# Revit family: Drain_Floor_12-Inch-Round_Zurn-Z1736_Extra-Heavy-Duty
name_source: partatom
category: Plumbing Fixtures
units: mm (PartAtom-declared; Revit-internal decimal feet)

## family parameters
Always vertical = Yes
Cut with Voids When Loaded = No
Maintain Annotation Orientation = No
OmniClass Number = 23.45.55.21
OmniClass Title = Drains (Wastes)
Part Type = Normal
Room Calculation Point = No
Round Connector Dimension = Use Radius
Shared = No
Work Plane-Based = No

## types (12) — shared parameters
Approx. Weight (Lbs) = 61 "
Assembly Code = D2030300
CW Connection = No
Default Elevation = 20 "
Description = 12 INCH DIAMETER EXTRA HEAVY-DUTY FLOOR DRAIN
Grate Open Area (Sq. In.) = 34 "
HW Connection = No
Manufacturer = Zurn Water, LLC
Manufacurer Brand = Zurn
Modified Date = 11/14/25
Product Documentation Link = https://files.zurn.com
Product Page URL = https://www.zurn.com
Product data url = https://www.bimobject.com
URL = www.zurn.com
Vent Connection = No
Waste Connection = Yes
zero-valued in all types: CWFU, HWFU, WFU

## per-type parameters (varying)
| type | Body HT Dim 'E' | Main Material | Model | Pipe Size 'A' (Inner Diameter) | Pipe Size 'A' (Inner Radius) | Pipe Size 'A' (Nominal Diameter) | Pipe Size 'A' (Nominal Radius) | Pipe Size 'A' (Outer Diameter) | Pipe Size 'A' (Outer Radius) | Type Comments |
| Z1736-3BW | 6 " | Steel - Zurn - Stainless - Type - 304 | Z1736 | 3.069 " | 1.535 " | 3 " | 1.5 " | 3.5 " | 1.75 " | Z1736 - 3 Inch Butt-Weld Outlet |
| Z1736-3IP | 6.082 " | Steel - Zurn - Stainless - Type - 304 | Z1736 | 3.069 " | 1.535 " | 3 " | 1.5 " | 3.5 " | 1.75 " | Z1736 - 3 Inch IP Threaded Outlet |
| Z1736-4BW | 6 " | Steel - Zurn - Stainless - Type - 304 | Z1736 | 4.026 " | 2.013 " | 4 " | 2 " | 4.5 " | 2.25 " | Z1736 - 4 Inch Butt-Weld Outlet |
| Z1736-4IP | 6.082 " | Steel - Zurn - Stainless - Type - 304 | Z1736 | 4.026 " | 2.013 " | 4 " | 2 " | 4.5 " | 2.25 " | Z1736 - 4 Inch IP Threaded Outlet |
| Z1736-6BW | 6 " | Steel - Zurn - Stainless - Type - 304 | Z1736 | 6.065 " | 3.033 " | 6 " | 3 " | 6.625 " | 3.313 " | Z1736 - 6 Inch Butt-Weld Outlet |
| Z1736-6IP | 6.082 " | Steel - Zurn - Stainless - Type - 304 | Z1736 | 6.065 " | 3.033 " | 6 " | 3 " | 6.625 " | 3.313 " | Z1736 - 6 Inch IP Threaded Outlet |
| ZM1736-3BW | 6 " | Steel - Zurn- Stainless - Type - 316 | ZM1736 | 3.069 " | 1.535 " | 3 " | 1.5 " | 3.5 " | 1.75 " | ZM1736 - 3 Inch Butt-Weld Outlet |
| ZM1736-3IP | 6.082 " | Steel - Zurn- Stainless - Type - 316 | ZM1736 | 3.069 " | 1.535 " | 3 " | 1.5 " | 3.5 " | 1.75 " | ZM1736 - 3 Inch IP Threaded Outlet |
| ZM1736-4BW | 6 " | Steel - Zurn- Stainless - Type - 316 | ZM1736 | 4.026 " | 2.013 " | 4 " | 2 " | 4.5 " | 2.25 " | ZM1736 - 4 Inch Butt-Weld Outlet |
| ZM1736-4IP | 6.082 " | Steel - Zurn- Stainless - Type - 316 | ZM1736 | 4.026 " | 2.013 " | 4 " | 2 " | 4.5 " | 2.25 " | ZM1736 - 4 Inch IP Threaded Outlet |
| ZM1736-6BW | 6 " | Steel - Zurn- Stainless - Type - 316 | ZM1736 | 6.065 " | 3.033 " | 6 " | 3 " | 6.625 " | 3.313 " | ZM1736 - 6 Inch Butt-Weld Outlet |
| ZM1736-6IP | 6.082 " | Steel - Zurn- Stainless - Type - 316 | ZM1736 | 6.065 " | 3.033 " | 6 " | 3 " | 6.625 " | 3.313 " | ZM1736 - 6 Inch IP Threaded Outlet |

## geometry (parser evidence)
native form markers: Sweep x4
no freeform markers — native parametric forms only
